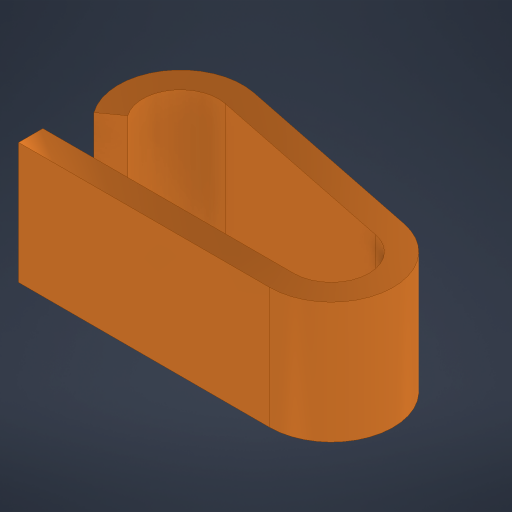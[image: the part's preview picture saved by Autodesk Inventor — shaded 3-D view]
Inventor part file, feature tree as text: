
AUTODESK INVENTOR PART (.ipt)
format: ipt  version: 2024.3 (Build 283343010, 343A)  size: 166,400 bytes
history: native  units: mm
features: extrude x1, sketch x1
ambient origin geometry x8: Origin, YZ Plane, XZ Plane, XY Plane, X Axis, Y Axis, Z Axis, Center Point
bodies: Volumenkörper1 (feature_tree)
feature tree (2):
  extrude  "Extrusion1"  Depth=1.0mm
  sketch  "Skizze1"  dims[d0=0.2mm d1=1.1mm d2=2.5mm d3=1.0mm d4=0.0mm]
